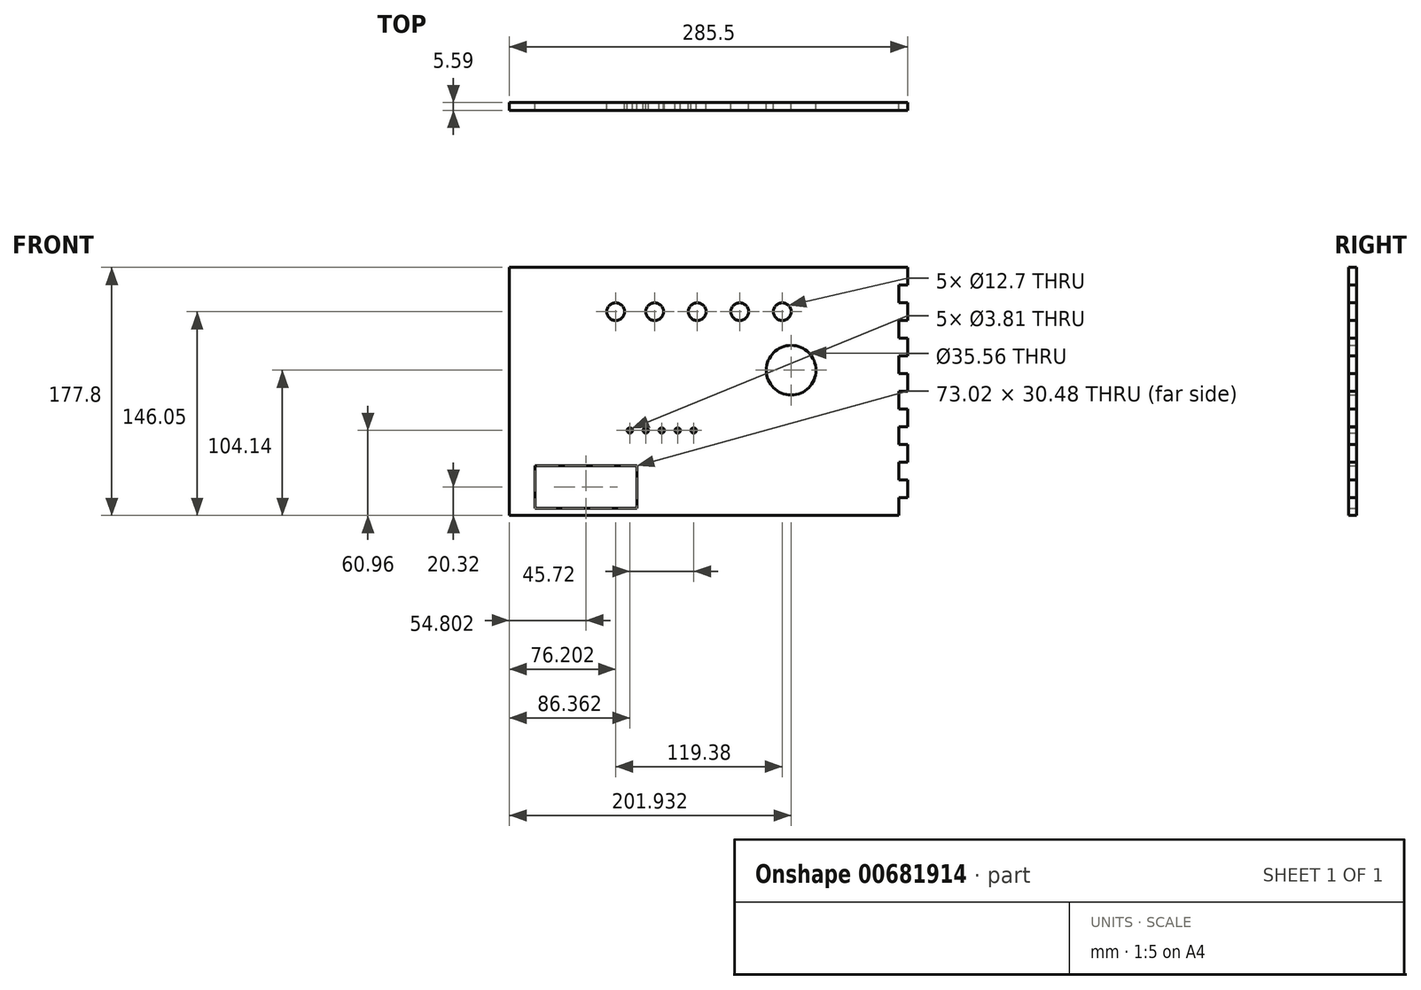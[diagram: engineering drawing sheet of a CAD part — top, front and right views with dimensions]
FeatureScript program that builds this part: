
annotation { "Feature Type Name" : "Feature", "Feature Type Description" : "" }
export const myFeature = defineFeature(function(context is Context, id is Id, definition is map)
    precondition{}
    {
        {
            var Q0;
            Q0=qCreatedBy(makeId("Front.planeOp"),FACE);
            var sketch = newSketch(context, id + "F0", { "sketchPlane" : qUnion([Q0])});
            skLineSegment(sketch, "E0.bottom", {"start": v(142.75, 88.9) * mm, "end": v(-142.75, 88.9) * mm});
            skLineSegment(sketch, "E0.top", {"start": v(142.75, -88.9) * mm, "end": v(-142.75, -88.9) * mm});
            skLineSegment(sketch, "E0.left", {"start": v(142.75, 88.9) * mm, "end": v(142.75, -88.9) * mm});
            skLineSegment(sketch, "E0.right", {"start": v(-142.75, 88.9) * mm, "end": v(-142.75, -88.9) * mm});
            skPoint(sketch, "E0.middle", {"position": v(0, 0) * mm});
            skSolve(sketch);
        }
        {
            var Q0;
            Q0=makeQuery(id+"F0.imprint","IMPRINT",FACE,{"disambiguationData":[TD([[makeQuery(id+"F0.imprint","IMPRINT",EDGE,{"derivedFrom":sQuery(id+"F0.wireOp",EDGE,"E0.bottom")}),1.0]])]});
            extrude(context, id + "F1", {"entities" : qUnion([Q0]), "depth" : 5.6 * mm, "offsetDistance" : 25.4 * mm});
        }
        {
            var Q0;
            Q0=qCreatedBy(makeId("Front.planeOp"),FACE);
            var sketch = newSketch(context, id + "F2", { "sketchPlane" : qUnion([Q0])});
            skLineSegment(sketch, "E1.bottom", {"start": v(-124.46, -53.34) * mm, "end": v(-51.44, -53.34) * mm});
            skLineSegment(sketch, "E1.top", {"start": v(-124.46, -83.82) * mm, "end": v(-51.43, -83.82) * mm});
            skLineSegment(sketch, "E1.left", {"start": v(-124.46, -53.34) * mm, "end": v(-124.46, -83.82) * mm});
            skLineSegment(sketch, "E1.right", {"start": v(-51.44, -53.34) * mm, "end": v(-51.43, -83.82) * mm});
            skPoint(sketch, "E1.middle", {"position": v(-87.95, -68.58) * mm});
            skSolve(sketch);
        }
        {
            var Q0;
            Q0=qSketchRegion(id+"F2",true);
            extrude(context, id + "F3", {"entities" : qUnion([Q0]), "operationType" : NewBodyOperationType.REMOVE, "depth" : 25.4 * mm, "offsetDistance" : 25.4 * mm});
        }
        {
            var Q0;
            Q0=qCreatedBy(makeId("Front.planeOp"),FACE);
            var sketch = newSketch(context, id + "F4", { "sketchPlane" : qUnion([Q0])});
            skPoint(sketch, "E2", {"position": v(-66.55, 57.15) * mm});
            skSolve(sketch);
        }
        {
            var Q0;
            Q0=sQuery(id+"F4.wireOp",VERTEX,"E2");
            var Q1;
            Q1=makeQuery(id+"F1.opExtrude","SWEPT_BODY",BODY,{"disambiguationData":[OSD([sQuery(id+"F0.wireOp",EDGE,"E0.bottom"),sQuery(id+"F0.wireOp",EDGE,"E0.top"),sQuery(id+"F0.wireOp",EDGE,"E0.left"),sQuery(id+"F0.wireOp",EDGE,"E0.right")])]});
            hole(context, id + "F5", {"style" : HoleStyle.SIMPLE, "endStyle" : HoleEndStyle.THROUGH, "oppositeDirection" : true, "holeDiameter" : 12.7 * mm, "majorDiameter" : 6.35 * mm, "isTappedThrough" : true, "tappedDepth" : 12.7 * mm, "tapClearance" : 3, "locations" : qUnion([Q0]), "scope" : qUnion([Q1])});
        }
        {
            var Q0;
            Q0=qCreatedBy(makeId("Front.planeOp"),FACE);
            var sketch = newSketch(context, id + "F6", { "sketchPlane" : qUnion([Q0])});
            skPoint(sketch, "E3", {"position": v(-38.6, 57.15) * mm});
            skPoint(sketch, "E4", {"position": v(-8.13, 57.15) * mm});
            skPoint(sketch, "E5", {"position": v(22.35, 57.15) * mm});
            skPoint(sketch, "E6", {"position": v(52.83, 57.15) * mm});
            skSolve(sketch);
        }
        {
            var Q0;
            Q0=sQuery(id+"F6.wireOp",VERTEX,"E3");
            var Q1;
            Q1=sQuery(id+"F6.wireOp",VERTEX,"E4");
            var Q2;
            Q2=sQuery(id+"F6.wireOp",VERTEX,"E5");
            var Q3;
            Q3=sQuery(id+"F6.wireOp",VERTEX,"E6");
            var Q4;
            Q4=makeQuery(id+"F1.opExtrude","SWEPT_BODY",BODY,{"disambiguationData":[OSD([sQuery(id+"F0.wireOp",EDGE,"E0.bottom"),sQuery(id+"F0.wireOp",EDGE,"E0.top"),sQuery(id+"F0.wireOp",EDGE,"E0.left"),sQuery(id+"F0.wireOp",EDGE,"E0.right")])]});
            hole(context, id + "F7", {"style" : HoleStyle.SIMPLE, "endStyle" : HoleEndStyle.THROUGH, "oppositeDirection" : true, "holeDiameter" : 12.7 * mm, "majorDiameter" : 6.35 * mm, "isTappedThrough" : true, "tappedDepth" : 12.7 * mm, "tapClearance" : 3, "locations" : qUnion([Q0, Q1, Q2, Q3]), "scope" : qUnion([Q4])});
        }
        {
            var Q0;
            Q0=qCreatedBy(makeId("Front.planeOp"),FACE);
            var sketch = newSketch(context, id + "F8", { "sketchPlane" : qUnion([Q0])});
            skPoint(sketch, "E7", {"position": v(-56.39, -27.94) * mm});
            skPoint(sketch, "E8", {"position": v(-44.96, -27.94) * mm});
            skPoint(sketch, "E9", {"position": v(-33.53, -27.94) * mm});
            skPoint(sketch, "E10", {"position": v(-22.1, -27.94) * mm});
            skPoint(sketch, "E11", {"position": v(-10.67, -27.94) * mm});
            skSolve(sketch);
        }
        {
            var Q0;
            Q0=sQuery(id+"F8.wireOp",VERTEX,"E7");
            var Q1;
            Q1=sQuery(id+"F8.wireOp",VERTEX,"E8");
            var Q2;
            Q2=sQuery(id+"F8.wireOp",VERTEX,"E9");
            var Q3;
            Q3=sQuery(id+"F8.wireOp",VERTEX,"E10");
            var Q4;
            Q4=sQuery(id+"F8.wireOp",VERTEX,"E11");
            var Q5;
            Q5=makeQuery(id+"F1.opExtrude","SWEPT_BODY",BODY,{"disambiguationData":[OSD([sQuery(id+"F0.wireOp",EDGE,"E0.bottom"),sQuery(id+"F0.wireOp",EDGE,"E0.top"),sQuery(id+"F0.wireOp",EDGE,"E0.left"),sQuery(id+"F0.wireOp",EDGE,"E0.right")])]});
            hole(context, id + "F9", {"style" : HoleStyle.SIMPLE, "endStyle" : HoleEndStyle.THROUGH, "oppositeDirection" : true, "holeDiameter" : 3.8 * mm, "majorDiameter" : 6.35 * mm, "isTappedThrough" : true, "tappedDepth" : 12.7 * mm, "tapClearance" : 3, "locations" : qUnion([Q0, Q1, Q2, Q3, Q4]), "scope" : qUnion([Q5])});
        }
        {
            var Q0;
            Q0=qCreatedBy(makeId("Front.planeOp"),FACE);
            var sketch = newSketch(context, id + "F10", { "sketchPlane" : qUnion([Q0])});
            skLineSegment(sketch, "E12.bottom", {"start": v(142.75, 76.2) * mm, "end": v(136.4, 76.2) * mm});
            skLineSegment(sketch, "E12.top", {"start": v(142.75, 63.5) * mm, "end": v(136.4, 63.5) * mm});
            skLineSegment(sketch, "E12.left", {"start": v(142.75, 76.2) * mm, "end": v(142.75, 63.5) * mm});
            skLineSegment(sketch, "E12.right", {"start": v(136.4, 76.2) * mm, "end": v(136.4, 63.5) * mm});
            skLineSegment(sketch, "E13.bottom", {"start": v(142.75, 25.4) * mm, "end": v(136.4, 25.4) * mm});
            skLineSegment(sketch, "E13.top", {"start": v(142.75, 12.7) * mm, "end": v(136.4, 12.7) * mm});
            skLineSegment(sketch, "E13.left", {"start": v(142.75, 25.4) * mm, "end": v(142.75, 12.7) * mm});
            skLineSegment(sketch, "E13.right", {"start": v(136.4, 25.4) * mm, "end": v(136.4, 12.7) * mm});
            skLineSegment(sketch, "E14.bottom", {"start": v(142.75, 0) * mm, "end": v(136.4, 0) * mm});
            skLineSegment(sketch, "E14.top", {"start": v(142.75, -12.7) * mm, "end": v(136.4, -12.7) * mm});
            skLineSegment(sketch, "E14.left", {"start": v(142.75, 0) * mm, "end": v(142.75, -12.7) * mm});
            skLineSegment(sketch, "E14.right", {"start": v(136.4, 0) * mm, "end": v(136.4, -12.7) * mm});
            skLineSegment(sketch, "E15.bottom", {"start": v(142.75, -25.4) * mm, "end": v(136.4, -25.4) * mm});
            skLineSegment(sketch, "E15.top", {"start": v(142.75, -38.1) * mm, "end": v(136.4, -38.1) * mm});
            skLineSegment(sketch, "E15.left", {"start": v(142.75, -25.4) * mm, "end": v(142.75, -38.1) * mm});
            skLineSegment(sketch, "E15.right", {"start": v(136.4, -25.4) * mm, "end": v(136.4, -38.1) * mm});
            skLineSegment(sketch, "E16.bottom", {"start": v(142.75, -50.8) * mm, "end": v(136.4, -50.8) * mm});
            skLineSegment(sketch, "E16.top", {"start": v(142.75, -63.5) * mm, "end": v(136.4, -63.5) * mm});
            skLineSegment(sketch, "E16.left", {"start": v(142.75, -50.8) * mm, "end": v(142.75, -63.5) * mm});
            skLineSegment(sketch, "E16.right", {"start": v(136.4, -50.8) * mm, "end": v(136.4, -63.5) * mm});
            skLineSegment(sketch, "E17.bottom", {"start": v(142.75, -76.2) * mm, "end": v(136.4, -76.2) * mm});
            skLineSegment(sketch, "E17.top", {"start": v(142.75, -88.9) * mm, "end": v(136.4, -88.9) * mm});
            skLineSegment(sketch, "E17.left", {"start": v(142.75, -76.2) * mm, "end": v(142.75, -88.9) * mm});
            skLineSegment(sketch, "E17.right", {"start": v(136.4, -76.2) * mm, "end": v(136.4, -88.9) * mm});
            skLineSegment(sketch, "E18.bottom", {"start": v(142.75, 50.8) * mm, "end": v(136.4, 50.8) * mm});
            skLineSegment(sketch, "E18.top", {"start": v(142.75, 38.1) * mm, "end": v(136.4, 38.1) * mm});
            skLineSegment(sketch, "E18.left", {"start": v(142.75, 50.8) * mm, "end": v(142.75, 38.1) * mm});
            skLineSegment(sketch, "E18.right", {"start": v(136.4, 50.8) * mm, "end": v(136.4, 38.1) * mm});
            skSolve(sketch);
        }
        {
            var Q0;
            Q0=qSketchRegion(id+"F10",true);
            extrude(context, id + "F11", {"entities" : qUnion([Q0]), "operationType" : NewBodyOperationType.REMOVE, "depth" : 25.4 * mm, "offsetDistance" : 25.4 * mm});
        }
        {
            var Q0;
            Q0=qCreatedBy(makeId("Front.planeOp"),FACE);
            var sketch = newSketch(context, id + "F12", { "sketchPlane" : qUnion([Q0])});
            skCircle(sketch, "E19", {"center": v(59.18, 15.24) * mm, "radius": 17.78 * mm});
            skSolve(sketch);
        }
        {
            var Q0;
            Q0=qSketchRegion(id+"F12",true);
            extrude(context, id + "F13", {"entities" : qUnion([Q0]), "operationType" : NewBodyOperationType.REMOVE, "depth" : 25.4 * mm, "offsetDistance" : 25.4 * mm});
        }
    });
